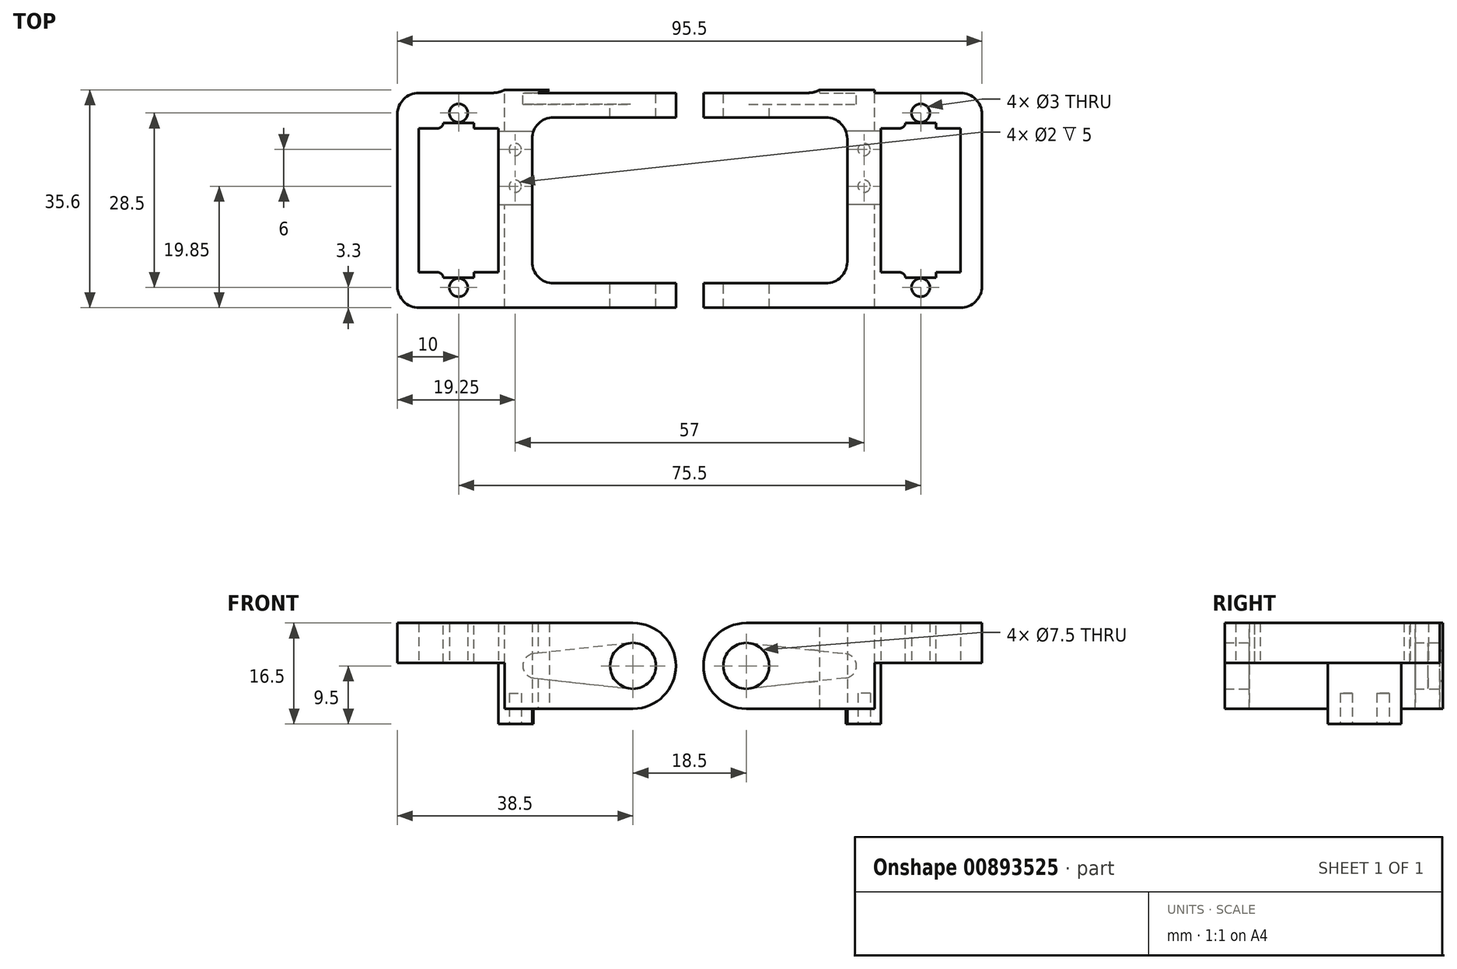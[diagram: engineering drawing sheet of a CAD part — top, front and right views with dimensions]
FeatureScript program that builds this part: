
annotation { "Feature Type Name" : "Feature", "Feature Type Description" : "" }
export const myFeature = defineFeature(function(context is Context, id is Id, definition is map)
    precondition{}
    {
        {
            var Q0;
            Q0=qCreatedBy(makeId("Top.planeOp"),FACE);
            var sketch = newSketch(context, id + "F0", { "sketchPlane" : qUnion([Q0])});
            skLineSegment(sketch, "E0.bottom", {"start": v(22.75, 17.55) * mm, "end": v(-22.75, 17.55) * mm});
            skLineSegment(sketch, "E0.top", {"start": v(22.75, -17.55) * mm, "end": v(-22.75, -17.55) * mm});
            skLineSegment(sketch, "E0.left", {"start": v(22.75, 17.55) * mm, "end": v(22.75, -17.55) * mm});
            skLineSegment(sketch, "E0.right", {"start": v(-22.75, 17.55) * mm, "end": v(-22.75, -17.55) * mm});
            skPoint(sketch, "E0.middle", {"position": v(0, 0) * mm});
            skLineSegment(sketch, "E1.bottom", {"start": v(22.75, 13.55) * mm, "end": v(-0.75, 13.55) * mm});
            skLineSegment(sketch, "E1.top", {"start": v(22.75, -13.55) * mm, "end": v(-0.75, -13.55) * mm});
            skLineSegment(sketch, "E1.left", {"start": v(22.75, 13.55) * mm, "end": v(22.75, -13.55) * mm});
            skLineSegment(sketch, "E1.right", {"start": v(-0.75, 13.55) * mm, "end": v(-0.75, -13.55) * mm});
            skLineSegment(sketch, "E2", {"start": v(0, 0) * mm, "end": v(-0.75, 0) * mm, "construction": true});
            skSolve(sketch);
        }
        {
            var Q0;
            {var subQ1=sQuery(id+"F0.wireOp",EDGE,"E0.bottom");Q0=makeQuery(id+"F0.imprint","IMPRINT",FACE,{"disambiguationData":[TD([[makeQuery(id+"F0.imprint","IMPRINT",EDGE,{"derivedFrom":subQ1}),1.0]])]});}
            extrude(context, id + "F1", {"entities" : qUnion([Q0]), "depth" : 14 * mm, "offsetDistance" : 25 * mm});
        }
        {
            var Q0;
            Q0=makeQuery(id+"F1.opExtrude","CAP_FACE",FACE,{"disambiguationData":[OSD([sQuery(id+"F0.wireOp",EDGE,"E0.bottom"),sQuery(id+"F0.wireOp",EDGE,"E0.top"),sQuery(id+"F0.wireOp",EDGE,"E0.left"),sQuery(id+"F0.wireOp",EDGE,"E0.right"),sQuery(id+"F0.wireOp",EDGE,"E1.bottom"),sQuery(id+"F0.wireOp",EDGE,"E1.top"),sQuery(id+"F0.wireOp",EDGE,"E1.right")])],"isStart":true});
            var sketch = newSketch(context, id + "F2", { "sketchPlane" : qUnion([Q0])});
            skLineSegment(sketch, "E3.bottom", {"start": v(-22.75, 17.55) * mm, "end": v(-5.25, 17.55) * mm});
            skLineSegment(sketch, "E3.top", {"start": v(-22.75, -17.55) * mm, "end": v(-5.25, -17.55) * mm});
            skLineSegment(sketch, "E3.left", {"start": v(-22.75, 17.55) * mm, "end": v(-22.75, -17.55) * mm});
            skLineSegment(sketch, "E3.right", {"start": v(-5.25, 17.55) * mm, "end": v(-5.25, -17.55) * mm});
            skSolve(sketch);
        }
        {
            var Q0;
            Q0 = qSketchRegion(id + "F2", true);
            extrude(context, id + "F3", {"entities" : qUnion([Q0]), "operationType" : NewBodyOperationType.REMOVE, "oppositeDirection" : true, "depth" : 7.5 * mm, "offsetDistance" : 25 * mm});
        }
        {
            var Q0;
            Q0=makeQuery(id+"F3.boolean.opBoolean","COPY",FACE,{"derivedFrom":makeQuery(id+"F3.opExtrude","CAP_FACE",FACE,{"disambiguationData":[OSD([sQuery(id+"F2.wireOp",EDGE,"E3.bottom"),sQuery(id+"F2.wireOp",EDGE,"E3.top"),sQuery(id+"F2.wireOp",EDGE,"E3.left"),sQuery(id+"F2.wireOp",EDGE,"E3.right")])],"isStart":false})});
            var sketch = newSketch(context, id + "F4", { "sketchPlane" : qUnion([Q0])});
            skLineSegment(sketch, "E4.bottom", {"start": v(-6.25, 11.75) * mm, "end": v(-19.25, 11.75) * mm});
            skLineSegment(sketch, "E4.top", {"start": v(-6.25, -11.75) * mm, "end": v(-19.25, -11.75) * mm});
            skLineSegment(sketch, "E4.left", {"start": v(-6.25, 11.75) * mm, "end": v(-6.25, -11.75) * mm});
            skLineSegment(sketch, "E4.right", {"start": v(-19.25, 11.75) * mm, "end": v(-19.25, -11.75) * mm});
            skPoint(sketch, "E4.middle", {"position": v(-12.75, 0) * mm});
            skSolve(sketch);
        }
        {
            var Q0;
            Q0 = qSketchRegion(id + "F4", true);
            extrude(context, id + "F5", {"entities" : qUnion([Q0]), "operationType" : NewBodyOperationType.REMOVE, "oppositeDirection" : true, "depth" : 25 * mm, "offsetDistance" : 25 * mm});
        }
        {
            var Q0;
            Q0=makeQuery(id+"F3.boolean.opBoolean","COPY",FACE,{"derivedFrom":makeQuery(id+"F3.opExtrude","CAP_FACE",FACE,{"disambiguationData":[OSD([sQuery(id+"F2.wireOp",EDGE,"E3.bottom"),sQuery(id+"F2.wireOp",EDGE,"E3.top"),sQuery(id+"F2.wireOp",EDGE,"E3.left"),sQuery(id+"F2.wireOp",EDGE,"E3.right")])],"isStart":false})});
            var sketch = newSketch(context, id + "F6", { "sketchPlane" : qUnion([Q0])});
            skLineSegment(sketch, "E5.bottom", {"start": v(-6.25, -11.3) * mm, "end": v(-5.25, -11.3) * mm});
            skLineSegment(sketch, "E5.top", {"start": v(-6.25, 0.7) * mm, "end": v(-5.25, 0.7) * mm});
            skLineSegment(sketch, "E5.left", {"start": v(-6.25, -11.3) * mm, "end": v(-6.25, 0.7) * mm});
            skLineSegment(sketch, "E5.right", {"start": v(-5.25, -11.3) * mm, "end": v(-5.25, 0.7) * mm});
            skSolve(sketch);
        }
        {
            var Q0;
            Q0 = qSketchRegion(id + "F6", true);
            extrude(context, id + "F7", {"entities" : qUnion([Q0]), "operationType" : NewBodyOperationType.ADD, "depth" : 10 * mm, "offsetDistance" : 25 * mm});
        }
        {
            var Q0;
            Q0=makeQuery(id+"F1.opExtrude","CAP_FACE",FACE,{"disambiguationData":[OSD([sQuery(id+"F0.wireOp",EDGE,"E0.bottom"),sQuery(id+"F0.wireOp",EDGE,"E0.top"),sQuery(id+"F0.wireOp",EDGE,"E0.left"),sQuery(id+"F0.wireOp",EDGE,"E0.right"),sQuery(id+"F0.wireOp",EDGE,"E1.bottom"),sQuery(id+"F0.wireOp",EDGE,"E1.top"),sQuery(id+"F0.wireOp",EDGE,"E1.right")])],"isStart":true});
            var sketch = newSketch(context, id + "F8", { "sketchPlane" : qUnion([Q0])});
            skLineSegment(sketch, "E6.bottom", {"start": v(-5.25, -11.3) * mm, "end": v(-0.75, -11.3) * mm});
            skLineSegment(sketch, "E6.top", {"start": v(-5.25, 0.7) * mm, "end": v(-0.75, 0.7) * mm});
            skLineSegment(sketch, "E6.left", {"start": v(-5.25, -11.3) * mm, "end": v(-5.25, 0.7) * mm});
            skLineSegment(sketch, "E6.right", {"start": v(-0.75, -11.3) * mm, "end": v(-0.75, 0.7) * mm});
            skSolve(sketch);
        }
        {
            var Q0;
            Q0 = qSketchRegion(id + "F8", true);
            var Q1;
            Q1=makeQuery(id+"F7.opExtrude","CAP_FACE",FACE,{"disambiguationData":[OSD([sQuery(id+"F6.wireOp",EDGE,"E5.bottom"),sQuery(id+"F6.wireOp",EDGE,"E5.top"),sQuery(id+"F6.wireOp",EDGE,"E5.left"),sQuery(id+"F6.wireOp",EDGE,"E5.right")])],"isStart":false});
            extrude(context, id + "F9", {"entities" : qUnion([Q0]), "operationType" : NewBodyOperationType.ADD, "endBound" : BoundingType.UP_TO_SURFACE, "depth" : 25 * mm, "endBoundEntityFace" : qUnion([Q1]), "offsetDistance" : 25 * mm});
        }
        {
            var Q0;
            {var subQ0=sQuery(id+"F0.wireOp",EDGE,"E0.left");Q0=makeQuery(id+"F1.opExtrude","CAP_EDGE",EDGE,{"disambiguationData":[OSD([subQ0]),TDD([makeQuery(id+"F0.imprint","IMPRINT",EDGE,{"disambiguationData":[TD([[makeQuery(id+"F0.imprint","INTERSECT",VERTEX,{"derivedFrom":[sQuery(id+"F0.wireOp",EDGE,"E0.top"),subQ0]}),1.0]])],"derivedFrom":subQ0})])],"isStart":false});}
            var Q1;
            {var subQ0=sQuery(id+"F0.wireOp",EDGE,"E0.left");Q1=makeQuery(id+"F1.opExtrude","CAP_EDGE",EDGE,{"disambiguationData":[OSD([subQ0]),TDD([makeQuery(id+"F0.imprint","IMPRINT",EDGE,{"disambiguationData":[TD([[makeQuery(id+"F0.imprint","INTERSECT",VERTEX,{"derivedFrom":[sQuery(id+"F0.wireOp",EDGE,"E0.top"),subQ0]}),1.0]])],"derivedFrom":subQ0})])],"isStart":true});}
            var Q2;
            {var subQ0=sQuery(id+"F0.wireOp",EDGE,"E0.left");Q2=makeQuery(id+"F1.opExtrude","CAP_EDGE",EDGE,{"disambiguationData":[OSD([subQ0]),TDD([makeQuery(id+"F0.imprint","IMPRINT",EDGE,{"disambiguationData":[TD([[makeQuery(id+"F0.imprint","INTERSECT",VERTEX,{"derivedFrom":[sQuery(id+"F0.wireOp",EDGE,"E0.bottom"),subQ0]}),-1.0]])],"derivedFrom":subQ0})])],"isStart":false});}
            var Q3;
            {var subQ0=sQuery(id+"F0.wireOp",EDGE,"E0.left");Q3=makeQuery(id+"F1.opExtrude","CAP_EDGE",EDGE,{"disambiguationData":[OSD([subQ0]),TDD([makeQuery(id+"F0.imprint","IMPRINT",EDGE,{"disambiguationData":[TD([[makeQuery(id+"F0.imprint","INTERSECT",VERTEX,{"derivedFrom":[sQuery(id+"F0.wireOp",EDGE,"E0.bottom"),subQ0]}),-1.0]])],"derivedFrom":subQ0})])],"isStart":true});}
            fillet(context, id + "F10", {"entities" : qUnion([Q0, Q1, Q2, Q3]), "radius" : 7 * mm, "tangentPropagation" : true, "defaultsChanged" : true, "vertexSettings" : [], "allowEdgeOverflow" : false});
        }
        {
            var Q0;
            Q0=makeQuery(id+"F1.opExtrude","SWEPT_EDGE",EDGE,{"disambiguationData":[OSD([sQuery(id+"F0.wireOp",EDGE,"E0.top"),sQuery(id+"F0.wireOp",EDGE,"E0.right")])]});
            var Q1;
            Q1=makeQuery(id+"F1.opExtrude","SWEPT_EDGE",EDGE,{"disambiguationData":[OSD([sQuery(id+"F0.wireOp",EDGE,"E0.bottom"),sQuery(id+"F0.wireOp",EDGE,"E0.right")])]});
            fillet(context, id + "F11", {"entities" : qUnion([Q0, Q1]), "radius" : 3.5 * mm, "tangentPropagation" : true, "allowEdgeOverflow" : false});
        }
        {
            var Q0;
            Q0=makeQuery(id+"F1.opExtrude","SWEPT_FACE",FACE,{"disambiguationData":[OSD([sQuery(id+"F0.wireOp",EDGE,"E0.bottom")])]});
            var sketch = newSketch(context, id + "F12", { "sketchPlane" : qUnion([Q0])});
            skCircle(sketch, "E7", {"center": v(-15.75, 7) * mm, "radius": 3.75 * mm});
            skSolve(sketch);
        }
        {
            var Q0;
            Q0 = qSketchRegion(id + "F12", true);
            extrude(context, id + "F13", {"entities" : qUnion([Q0]), "operationType" : NewBodyOperationType.REMOVE, "endBound" : BoundingType.THROUGH_ALL, "oppositeDirection" : true, "depth" : 25 * mm, "offsetDistance" : 25 * mm});
        }
        {
            var Q0;
            Q0=makeQuery(id+"F1.opExtrude","SWEPT_FACE",FACE,{"disambiguationData":[OSD([sQuery(id+"F0.wireOp",EDGE,"E0.bottom")])]});
            var sketch = newSketch(context, id + "F14", { "sketchPlane" : qUnion([Q0])});
            skLineSegment(sketch, "E8", {"start": v(-19.5, 7) * mm, "end": v(0.25, 7) * mm, "construction": true});
            skPoint(sketch, "E8.startSnap0", {"position": v(-15.34, 7) * mm});
            skCircle(sketch, "E9", {"center": v(0.25, 7) * mm, "radius": 2 * mm});
            skLineSegment(sketch, "E10", {"start": v(0.47, 5.01) * mm, "end": v(-15.34, 3.27) * mm});
            skLineSegment(sketch, "E11", {"start": v(-15.34, 10.73) * mm, "end": v(0.47, 8.99) * mm});
            skLineSegment(sketch, "E12", {"start": v(-15.34, 10.73) * mm, "end": v(-15.34, 3.27) * mm, "construction": true});
            skSolve(sketch);
        }
        {
            var Q0;
            Q0 = qSketchRegion(id + "F14", true);
            var Q1;
            {var subQ0=sQuery(id+"F14.wireOp",EDGE,"E10");Q1=makeQuery(id+"F14.imprint","IMPRINT",FACE,{"disambiguationData":[TD([[makeQuery(id+"F14.imprint","IMPRINT",EDGE,{"derivedFrom":subQ0}),-1.0]])]});}
            extrude(context, id + "F15", {"entities" : qUnion([Q0, Q1]), "operationType" : NewBodyOperationType.REMOVE, "oppositeDirection" : true, "depth" : 1.9 * mm, "offsetDistance" : 25 * mm});
        }
        {
            var Q0;
            Q0=makeQuery(id+"F3.boolean.opBoolean","COPY",FACE,{"derivedFrom":makeQuery(id+"F3.opExtrude","CAP_FACE",FACE,{"disambiguationData":[OSD([sQuery(id+"F2.wireOp",EDGE,"E3.bottom"),sQuery(id+"F2.wireOp",EDGE,"E3.top"),sQuery(id+"F2.wireOp",EDGE,"E3.left"),sQuery(id+"F2.wireOp",EDGE,"E3.right")])],"isStart":false})});
            var sketch = newSketch(context, id + "F16", { "sketchPlane" : qUnion([Q0])});
            skCircle(sketch, "E13", {"center": v(-12.75, -14.25) * mm, "radius": 1.5 * mm});
            skCircle(sketch, "E14", {"center": v(-12.75, 14.25) * mm, "radius": 1.5 * mm});
            skLineSegment(sketch, "E15", {"start": v(-12.75, -14.25) * mm, "end": v(-5.25, -14.25) * mm, "construction": true});
            skLineSegment(sketch, "E16", {"start": v(-12.75, -14.25) * mm, "end": v(-12.75, -17.55) * mm, "construction": true});
            skLineSegment(sketch, "E17", {"start": v(-12.75, 14.25) * mm, "end": v(-5.25, 14.25) * mm, "construction": true});
            skLineSegment(sketch, "E18", {"start": v(-12.75, 14.25) * mm, "end": v(-12.75, 17.55) * mm, "construction": true});
            skSolve(sketch);
        }
        {
            var Q0;
            Q0 = qSketchRegion(id + "F16", true);
            extrude(context, id + "F17", {"entities" : qUnion([Q0]), "operationType" : NewBodyOperationType.REMOVE, "oppositeDirection" : true, "depth" : 25 * mm, "offsetDistance" : 25 * mm});
        }
        {
            var Q0;
            Q0=makeQuery(id+"F9.boolean.opBoolean","MERGE",FACE,{"derivedFrom":[makeQuery(id+"F7.opExtrude","CAP_FACE",FACE,{"disambiguationData":[OSD([sQuery(id+"F6.wireOp",EDGE,"E5.bottom"),sQuery(id+"F6.wireOp",EDGE,"E5.top"),sQuery(id+"F6.wireOp",EDGE,"E5.left"),sQuery(id+"F6.wireOp",EDGE,"E5.right")])],"isStart":false}),makeQuery(id+"F9.opExtrude","CAP_FACE",FACE,{"disambiguationData":[OSD([sQuery(id+"F8.wireOp",EDGE,"E6.bottom"),sQuery(id+"F8.wireOp",EDGE,"E6.top"),sQuery(id+"F8.wireOp",EDGE,"E6.left"),sQuery(id+"F8.wireOp",EDGE,"E6.right")])],"isStart":false})]});
            var sketch = newSketch(context, id + "F18", { "sketchPlane" : qUnion([Q0])});
            skLineSegment(sketch, "E19", {"start": v(-3.5, 0.7) * mm, "end": v(-3.5, -2.3) * mm, "construction": true});
            skLineSegment(sketch, "E20", {"start": v(-3.5, -2.3) * mm, "end": v(-3.5, -8.3) * mm, "construction": true});
            skLineSegment(sketch, "E21", {"start": v(-3.5, -8.3) * mm, "end": v(-3.5, -11.3) * mm, "construction": true});
            skCircle(sketch, "E22", {"center": v(-3.5, -2.3) * mm, "radius": 1 * mm});
            skCircle(sketch, "E23", {"center": v(-3.5, -8.3) * mm, "radius": 1 * mm});
            skSolve(sketch);
        }
        {
            var Q0;
            Q0 = qSketchRegion(id + "F18", true);
            extrude(context, id + "F19", {"entities" : qUnion([Q0]), "operationType" : NewBodyOperationType.REMOVE, "oppositeDirection" : true, "depth" : 5 * mm, "offsetDistance" : 25 * mm});
        }
        {
            var Q0;
            Q0=qCreatedBy(makeId("Right.planeOp"),FACE);
            cPlane(context, id + "F20", {"entities" : qUnion([Q0]), "cplaneType" : CPlaneType.OFFSET, "offset" : 25 * mm, "width" : 150 * mm, "height" : 150 * mm});
        }
        {
            var Q0;
            Q0=makeQuery(id+"F1.opExtrude","SWEPT_BODY",BODY,{"disambiguationData":[OSD([sQuery(id+"F0.wireOp",EDGE,"E0.bottom"),sQuery(id+"F0.wireOp",EDGE,"E0.top"),sQuery(id+"F0.wireOp",EDGE,"E0.left"),sQuery(id+"F0.wireOp",EDGE,"E0.right"),sQuery(id+"F0.wireOp",EDGE,"E1.bottom"),sQuery(id+"F0.wireOp",EDGE,"E1.top"),sQuery(id+"F0.wireOp",EDGE,"E1.right")])]});
            var Q1;
            Q1=qCreatedBy(id+"F20.planeOp",FACE);
            mirror(context, id + "F21", {"entities" : qUnion([Q0]), "mirrorPlane" : qUnion([Q1])});
        }
        {
            var Q0;
            Q0=makeQuery(id+"F21.opPattern","COPY",FACE,{"derivedFrom":makeQuery(id+"F1.opExtrude","SWEPT_FACE",FACE,{"disambiguationData":[OSD([sQuery(id+"F0.wireOp",EDGE,"E0.bottom")])]}),"instanceName":"1"});
            var sketch = newSketch(context, id + "F22", { "sketchPlane" : qUnion([Q0])});
            skLineSegment(sketch, "E24.bottom", {"start": v(-55.25, 0) * mm, "end": v(-46.25, 0) * mm});
            skLineSegment(sketch, "E24.top", {"start": v(-55.25, 14) * mm, "end": v(-46.25, 14) * mm});
            skLineSegment(sketch, "E24.left", {"start": v(-55.25, 0) * mm, "end": v(-55.25, 14) * mm});
            skLineSegment(sketch, "E24.right", {"start": v(-46.25, 0) * mm, "end": v(-46.25, 14) * mm});
            skLineSegment(sketch, "E25.bottom", {"start": v(5.25, 0) * mm, "end": v(-3.75, 0) * mm});
            skLineSegment(sketch, "E25.top", {"start": v(5.25, 14) * mm, "end": v(-3.75, 14) * mm});
            skLineSegment(sketch, "E25.left", {"start": v(5.25, 0) * mm, "end": v(5.25, 14) * mm});
            skLineSegment(sketch, "E25.right", {"start": v(-3.75, 0) * mm, "end": v(-3.75, 14) * mm});
            skSolve(sketch);
        }
        {
            var Q0;
            Q0 = qSketchRegion(id + "F22", true);
            extrude(context, id + "F23", {"entities" : qUnion([Q0]), "operationType" : NewBodyOperationType.ADD, "depth" : 0.5 * mm, "offsetDistance" : 25 * mm});
        }
        {
            var Q0;
            {var subQ0=sQuery(id+"F22.wireOp",EDGE,"E24.right");var subQ2=sQuery(id+"F0.wireOp",EDGE,"E0.bottom");var subQ3=makeQuery(id+"F21.opPattern","COPY",FACE,{"derivedFrom":makeQuery(id+"F1.opExtrude","SWEPT_FACE",FACE,{"disambiguationData":[OSD([subQ2])]}),"instanceName":"1"});var subQ4=makeQuery(id+"F23.opExtrude","SWEPT_FACE",FACE,{"disambiguationData":[OSD([subQ0])]});Q0=makeQuery(id+"F23.boolean.opBoolean","SPLIT",EDGE,{"disambiguationData":[topologyDisambiguationEdgeConnected([subQ3,subQ4]),TD([makeQuery(id+"F21.opPattern","COPY",FACE,{"derivedFrom":makeQuery(id+"F15.boolean.opBoolean","COPY",FACE,{"derivedFrom":makeQuery(id+"F15.opExtrude","SWEPT_FACE",FACE,{"disambiguationData":[OSD([sQuery(id+"F14.wireOp",EDGE,"E11")])]})}),"instanceName":"1"})])],"derivedFrom":makeQuery(id+"F23.opExtrude","CAP_EDGE",EDGE,{"disambiguationData":[OSD([subQ0])],"isStart":true})});}
            var Q1;
            {var subQ4=sQuery(id+"F0.wireOp",EDGE,"E0.bottom");var subQ5=makeQuery(id+"F1.opExtrude","SWEPT_FACE",FACE,{"disambiguationData":[OSD([subQ4])]});var subQ6=makeQuery(id+"F21.opPattern","COPY",FACE,{"derivedFrom":subQ5,"instanceName":"1"});var subQ7=sQuery(id+"F22.wireOp",EDGE,"E24.right");var subQ8=makeQuery(id+"F23.opExtrude","SWEPT_FACE",FACE,{"disambiguationData":[OSD([subQ7])]});Q1=makeQuery(id+"F23.boolean.opBoolean","SPLIT",EDGE,{"disambiguationData":[topologyDisambiguationEdgeConnected([subQ6,subQ8]),TD([makeQuery(id+"F21.opPattern","COPY",FACE,{"derivedFrom":makeQuery(id+"F15.boolean.opBoolean","COPY",FACE,{"derivedFrom":makeQuery(id+"F15.opExtrude","SWEPT_FACE",FACE,{"disambiguationData":[OSD([sQuery(id+"F14.wireOp",EDGE,"E10")])]})}),"instanceName":"1"})])],"derivedFrom":makeQuery(id+"F23.opExtrude","CAP_EDGE",EDGE,{"disambiguationData":[OSD([subQ7])],"isStart":true})});}
            var Q2;
            Q2=makeQuery(id+"F23.opExtrude","CAP_EDGE",EDGE,{"disambiguationData":[OSD([sQuery(id+"F22.wireOp",EDGE,"E24.left")])],"isStart":true});
            var Q3;
            {var subQ0=sQuery(id+"F22.wireOp",EDGE,"E25.right");var subQ2=sQuery(id+"F0.wireOp",EDGE,"E0.bottom");var subQ3=makeQuery(id+"F1.opExtrude","SWEPT_FACE",FACE,{"disambiguationData":[OSD([subQ2])]});var subQ4=makeQuery(id+"F23.opExtrude","SWEPT_FACE",FACE,{"disambiguationData":[OSD([subQ0])]});Q3=makeQuery(id+"F23.boolean.opBoolean","SPLIT",EDGE,{"disambiguationData":[topologyDisambiguationEdgeConnected([subQ3,subQ4]),TD([makeQuery(id+"F15.boolean.opBoolean","COPY",FACE,{"derivedFrom":makeQuery(id+"F15.opExtrude","SWEPT_FACE",FACE,{"disambiguationData":[OSD([sQuery(id+"F14.wireOp",EDGE,"E11")])]})})])],"derivedFrom":makeQuery(id+"F23.opExtrude","CAP_EDGE",EDGE,{"disambiguationData":[OSD([subQ0])],"isStart":true})});}
            var Q4;
            {var subQ1=sQuery(id+"F0.wireOp",EDGE,"E0.bottom");var subQ2=makeQuery(id+"F1.opExtrude","SWEPT_FACE",FACE,{"disambiguationData":[OSD([subQ1])]});var subQ3=sQuery(id+"F22.wireOp",EDGE,"E25.right");var subQ4=makeQuery(id+"F23.opExtrude","SWEPT_FACE",FACE,{"disambiguationData":[OSD([subQ3])]});Q4=makeQuery(id+"F23.boolean.opBoolean","SPLIT",EDGE,{"disambiguationData":[topologyDisambiguationEdgeConnected([subQ2,subQ4]),TD([makeQuery(id+"F15.boolean.opBoolean","COPY",FACE,{"derivedFrom":makeQuery(id+"F15.opExtrude","SWEPT_FACE",FACE,{"disambiguationData":[OSD([sQuery(id+"F14.wireOp",EDGE,"E10")])]})})])],"derivedFrom":makeQuery(id+"F23.opExtrude","CAP_EDGE",EDGE,{"disambiguationData":[OSD([subQ3])],"isStart":true})});}
            var Q5;
            Q5=makeQuery(id+"F23.opExtrude","CAP_EDGE",EDGE,{"disambiguationData":[OSD([sQuery(id+"F22.wireOp",EDGE,"E25.left")])],"isStart":true});
            var Q6;
            Q6=makeQuery(id+"F1.opExtrude","SWEPT_EDGE",EDGE,{"disambiguationData":[OSD([sQuery(id+"F0.wireOp",EDGE,"E1.top"),sQuery(id+"F0.wireOp",EDGE,"E1.right")])]});
            var Q7;
            Q7=makeQuery(id+"F1.opExtrude","SWEPT_EDGE",EDGE,{"disambiguationData":[OSD([sQuery(id+"F0.wireOp",EDGE,"E1.bottom"),sQuery(id+"F0.wireOp",EDGE,"E1.right")])]});
            var Q8;
            Q8=makeQuery(id+"F21.opPattern","COPY",EDGE,{"derivedFrom":makeQuery(id+"F1.opExtrude","SWEPT_EDGE",EDGE,{"disambiguationData":[OSD([sQuery(id+"F0.wireOp",EDGE,"E1.top"),sQuery(id+"F0.wireOp",EDGE,"E1.right")])]}),"instanceName":"1"});
            var Q9;
            Q9=makeQuery(id+"F21.opPattern","COPY",EDGE,{"derivedFrom":makeQuery(id+"F1.opExtrude","SWEPT_EDGE",EDGE,{"disambiguationData":[OSD([sQuery(id+"F0.wireOp",EDGE,"E1.bottom"),sQuery(id+"F0.wireOp",EDGE,"E1.right")])]}),"instanceName":"1"});
            fillet(context, id + "F24", {"entities" : qUnion([Q0, Q1, Q2, Q3, Q4, Q5, Q6, Q7, Q8, Q9]), "radius" : 3.5 * mm, "tangentPropagation" : true, "allowEdgeOverflow" : false});
        }
        {
            var Q0;
            Q0=makeQuery(id+"F23.boolean.opBoolean","MERGE",FACE,{"derivedFrom":[makeQuery(id+"F1.opExtrude","CAP_FACE",FACE,{"disambiguationData":[OSD([sQuery(id+"F0.wireOp",EDGE,"E0.bottom"),sQuery(id+"F0.wireOp",EDGE,"E0.top"),sQuery(id+"F0.wireOp",EDGE,"E0.left"),sQuery(id+"F0.wireOp",EDGE,"E0.right"),sQuery(id+"F0.wireOp",EDGE,"E1.bottom"),sQuery(id+"F0.wireOp",EDGE,"E1.top"),sQuery(id+"F0.wireOp",EDGE,"E1.right")])],"isStart":false}),makeQuery(id+"F23.opExtrude","SWEPT_FACE",FACE,{"disambiguationData":[OSD([sQuery(id+"F22.wireOp",EDGE,"E25.top")])]})]});
            var sketch = newSketch(context, id + "F25", { "sketchPlane" : qUnion([Q0])});
            skLineSegment(sketch, "E26.bottom", {"start": v(-15.25, 11.75) * mm, "end": v(-10.25, 11.75) * mm});
            skLineSegment(sketch, "E26.top", {"start": v(-15.25, 12.65) * mm, "end": v(-10.25, 12.65) * mm});
            skLineSegment(sketch, "E26.left", {"start": v(-10.25, 11.75) * mm, "end": v(-10.25, 12.65) * mm});
            skLineSegment(sketch, "E26.right", {"start": v(-15.25, 11.75) * mm, "end": v(-15.25, 12.65) * mm});
            skLineSegment(sketch, "E27.bottom", {"start": v(-15.25, -11.75) * mm, "end": v(-10.25, -11.75) * mm});
            skLineSegment(sketch, "E27.top", {"start": v(-15.25, -12.65) * mm, "end": v(-10.25, -12.65) * mm});
            skLineSegment(sketch, "E27.left", {"start": v(-15.25, -11.75) * mm, "end": v(-15.25, -12.65) * mm});
            skLineSegment(sketch, "E27.right", {"start": v(-10.25, -11.75) * mm, "end": v(-10.25, -12.65) * mm});
            skLineSegment(sketch, "E28.bottom", {"start": v(65.25, 11.75) * mm, "end": v(60.25, 11.75) * mm});
            skLineSegment(sketch, "E28.top", {"start": v(65.25, 12.65) * mm, "end": v(60.25, 12.65) * mm});
            skLineSegment(sketch, "E28.left", {"start": v(65.25, 11.75) * mm, "end": v(65.25, 12.65) * mm});
            skLineSegment(sketch, "E28.right", {"start": v(60.25, 11.75) * mm, "end": v(60.25, 12.65) * mm});
            skLineSegment(sketch, "E29.bottom", {"start": v(65.25, -11.75) * mm, "end": v(60.25, -11.75) * mm});
            skLineSegment(sketch, "E29.top", {"start": v(65.25, -12.65) * mm, "end": v(60.25, -12.65) * mm});
            skLineSegment(sketch, "E29.left", {"start": v(65.25, -11.75) * mm, "end": v(65.25, -12.65) * mm});
            skLineSegment(sketch, "E29.right", {"start": v(60.25, -11.75) * mm, "end": v(60.25, -12.65) * mm});
            skSolve(sketch);
        }
        {
            var Q0;
            Q0 = qSketchRegion(id + "F25", true);
            extrude(context, id + "F26", {"entities" : qUnion([Q0]), "operationType" : NewBodyOperationType.REMOVE, "oppositeDirection" : true, "depth" : 25 * mm, "offsetDistance" : 25 * mm});
        }
        {
            var Q0;
            Q0=makeQuery(id+"F26.boolean.opBoolean","COPY",EDGE,{"derivedFrom":makeQuery(id+"F26.opExtrude","SWEPT_EDGE",EDGE,{"disambiguationData":[OSD([sQuery(id+"F0.wireOp",EDGE,"E0.bottom"),sQuery(id+"F0.wireOp",EDGE,"E0.top"),sQuery(id+"F0.wireOp",EDGE,"E0.left"),sQuery(id+"F0.wireOp",EDGE,"E0.right"),sQuery(id+"F0.wireOp",EDGE,"E1.bottom"),sQuery(id+"F0.wireOp",EDGE,"E1.top"),sQuery(id+"F0.wireOp",EDGE,"E1.right"),sQuery(id+"F4.wireOp",EDGE,"E4.top"),sQuery(id+"F25.wireOp",EDGE,"E26.bottom"),sQuery(id+"F25.wireOp",EDGE,"E26.right")])]})});
            var Q1;
            Q1=makeQuery(id+"F26.boolean.opBoolean","COPY",EDGE,{"derivedFrom":makeQuery(id+"F26.opExtrude","SWEPT_EDGE",EDGE,{"disambiguationData":[OSD([sQuery(id+"F0.wireOp",EDGE,"E0.bottom"),sQuery(id+"F0.wireOp",EDGE,"E0.top"),sQuery(id+"F0.wireOp",EDGE,"E0.left"),sQuery(id+"F0.wireOp",EDGE,"E0.right"),sQuery(id+"F0.wireOp",EDGE,"E1.bottom"),sQuery(id+"F0.wireOp",EDGE,"E1.top"),sQuery(id+"F0.wireOp",EDGE,"E1.right"),sQuery(id+"F4.wireOp",EDGE,"E4.top"),sQuery(id+"F25.wireOp",EDGE,"E26.bottom"),sQuery(id+"F25.wireOp",EDGE,"E26.left")])]})});
            var Q2;
            Q2=makeQuery(id+"F26.boolean.opBoolean","COPY",EDGE,{"derivedFrom":makeQuery(id+"F26.opExtrude","SWEPT_EDGE",EDGE,{"disambiguationData":[OSD([sQuery(id+"F0.wireOp",EDGE,"E0.bottom"),sQuery(id+"F0.wireOp",EDGE,"E0.top"),sQuery(id+"F0.wireOp",EDGE,"E0.left"),sQuery(id+"F0.wireOp",EDGE,"E0.right"),sQuery(id+"F0.wireOp",EDGE,"E1.bottom"),sQuery(id+"F0.wireOp",EDGE,"E1.top"),sQuery(id+"F0.wireOp",EDGE,"E1.right"),sQuery(id+"F4.wireOp",EDGE,"E4.bottom"),sQuery(id+"F25.wireOp",EDGE,"E27.bottom"),sQuery(id+"F25.wireOp",EDGE,"E27.left")])]})});
            var Q3;
            Q3=makeQuery(id+"F26.boolean.opBoolean","COPY",EDGE,{"derivedFrom":makeQuery(id+"F26.opExtrude","SWEPT_EDGE",EDGE,{"disambiguationData":[OSD([sQuery(id+"F0.wireOp",EDGE,"E0.bottom"),sQuery(id+"F0.wireOp",EDGE,"E0.top"),sQuery(id+"F0.wireOp",EDGE,"E0.left"),sQuery(id+"F0.wireOp",EDGE,"E0.right"),sQuery(id+"F0.wireOp",EDGE,"E1.bottom"),sQuery(id+"F0.wireOp",EDGE,"E1.top"),sQuery(id+"F0.wireOp",EDGE,"E1.right"),sQuery(id+"F4.wireOp",EDGE,"E4.bottom"),sQuery(id+"F25.wireOp",EDGE,"E27.bottom"),sQuery(id+"F25.wireOp",EDGE,"E27.right")])]})});
            var Q4;
            Q4=makeQuery(id+"F26.boolean.opBoolean","COPY",EDGE,{"derivedFrom":makeQuery(id+"F26.opExtrude","SWEPT_EDGE",EDGE,{"disambiguationData":[OSD([sQuery(id+"F25.wireOp",EDGE,"E28.bottom"),sQuery(id+"F25.wireOp",EDGE,"E28.left")])]})});
            var Q5;
            Q5=makeQuery(id+"F26.boolean.opBoolean","COPY",EDGE,{"derivedFrom":makeQuery(id+"F26.opExtrude","SWEPT_EDGE",EDGE,{"disambiguationData":[OSD([sQuery(id+"F25.wireOp",EDGE,"E29.bottom"),sQuery(id+"F25.wireOp",EDGE,"E29.left")])]})});
            var Q6;
            Q6=makeQuery(id+"F26.boolean.opBoolean","COPY",EDGE,{"derivedFrom":makeQuery(id+"F26.opExtrude","SWEPT_EDGE",EDGE,{"disambiguationData":[OSD([sQuery(id+"F25.wireOp",EDGE,"E28.bottom"),sQuery(id+"F25.wireOp",EDGE,"E28.right")])]})});
            var Q7;
            Q7=makeQuery(id+"F26.boolean.opBoolean","COPY",EDGE,{"derivedFrom":makeQuery(id+"F26.opExtrude","SWEPT_EDGE",EDGE,{"disambiguationData":[OSD([sQuery(id+"F25.wireOp",EDGE,"E29.bottom"),sQuery(id+"F25.wireOp",EDGE,"E29.right")])]})});
            fillet(context, id + "F27", {"entities" : qUnion([Q0, Q1, Q2, Q3, Q4, Q5, Q6, Q7]), "tangentPropagation" : true, "radius" : 1 * mm, "defaultsChanged" : true, "vertexSettings" : [], "allowEdgeOverflow" : false});
        }
    });
